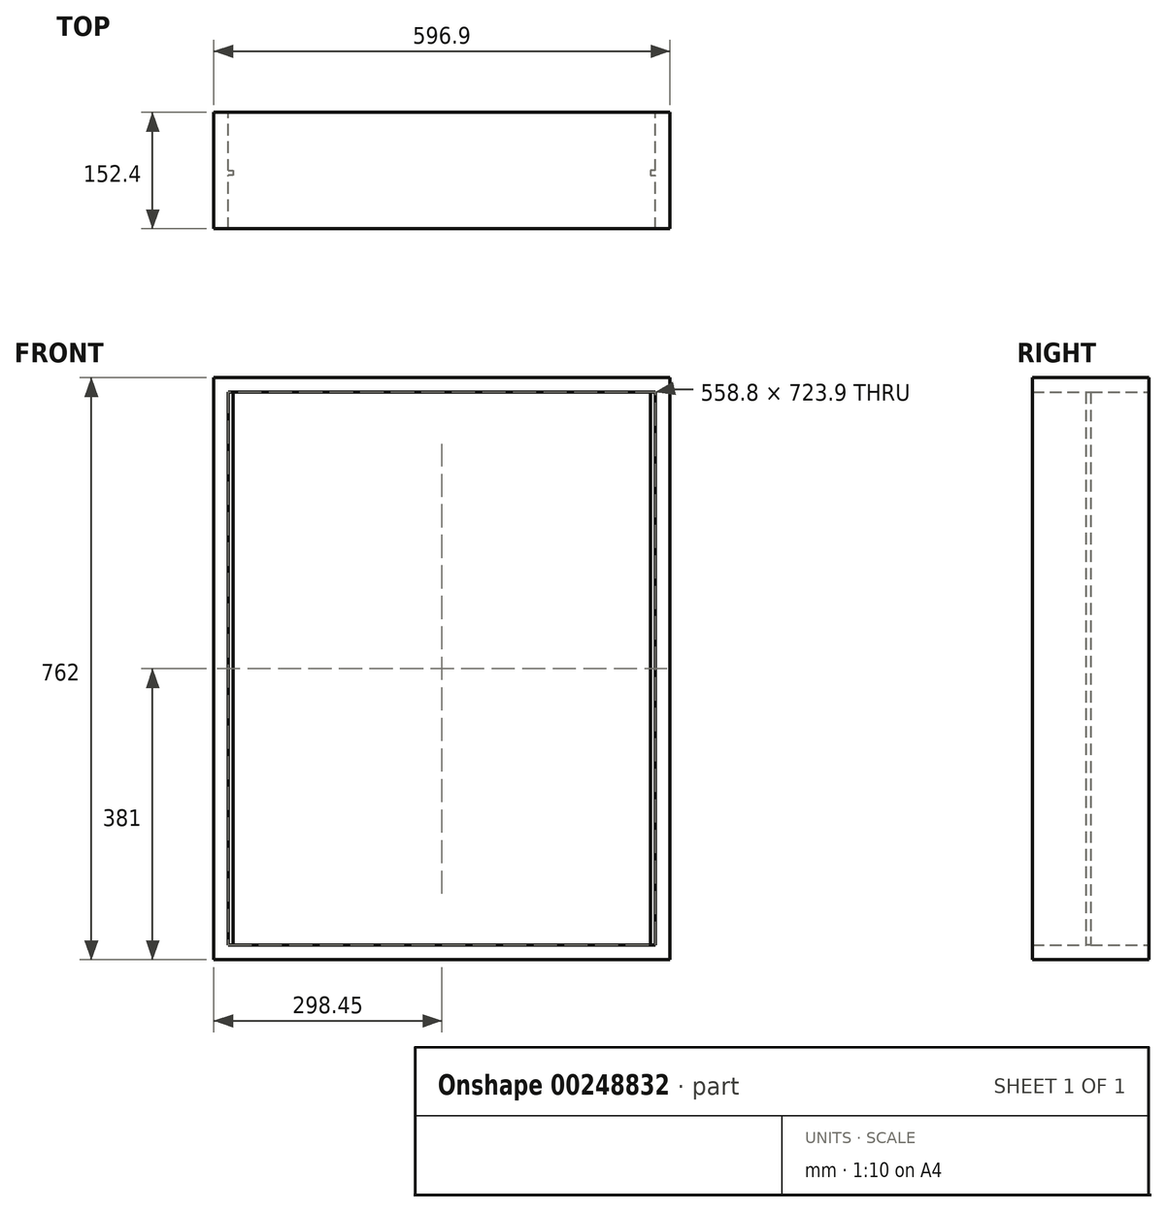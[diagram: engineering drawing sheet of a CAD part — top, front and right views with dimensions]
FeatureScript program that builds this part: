
annotation { "Feature Type Name" : "Feature", "Feature Type Description" : "" }
export const myFeature = defineFeature(function(context is Context, id is Id, definition is map)
    precondition{}
    {
        {
            var Q0;
            Q0=qCreatedBy(makeId("Front.planeOp"),FACE);
            var sketch = newSketch(context, id + "F0", { "sketchPlane" : qUnion([Q0])});
            skLineSegment(sketch, "E0.bottom", {"start": v(0, 0) * mm, "end": v(-558.8, 0) * mm});
            skLineSegment(sketch, "E0.top", {"start": v(0, 723.9) * mm, "end": v(-558.8, 723.9) * mm});
            skLineSegment(sketch, "E0.left", {"start": v(0, 0) * mm, "end": v(0, 723.9) * mm});
            skLineSegment(sketch, "E0.right", {"start": v(-558.8, 0) * mm, "end": v(-558.8, 723.9) * mm});
            skLineSegment(sketch, "E1.bottom", {"start": v(-577.85, 742.95) * mm, "end": v(19.05, 742.95) * mm});
            skLineSegment(sketch, "E1.top", {"start": v(-577.85, -19.05) * mm, "end": v(19.05, -19.05) * mm});
            skLineSegment(sketch, "E1.left", {"start": v(-577.85, 742.95) * mm, "end": v(-577.85, -19.05) * mm});
            skLineSegment(sketch, "E1.right", {"start": v(19.05, 742.95) * mm, "end": v(19.05, -19.05) * mm});
            skSolve(sketch);
        }
        {
            var Q0;
            Q0=makeQuery(id+"F0.imprint","IMPRINT",FACE,{"disambiguationData":[TD([[makeQuery(id+"F0.imprint","IMPRINT",EDGE,{"derivedFrom":sQuery(id+"F0.wireOp",EDGE,"E0.bottom")}),1.0]])]});
            extrude(context, id + "F1", {"entities" : qUnion([Q0]), "depth" : 152.4 * mm});
        }
        {
            var Q0;
            Q0=makeQuery(id+"F1.opExtrude","SWEPT_FACE",FACE,{"disambiguationData":[OSD([sQuery(id+"F0.wireOp",EDGE,"E0.bottom")])]});
            var sketch = newSketch(context, id + "F2", { "sketchPlane" : qUnion([Q0])});
            skLineSegment(sketch, "E2", {"start": v(-558.8, -76.2) * mm, "end": v(-552.45, -76.2) * mm});
            skLineSegment(sketch, "E3", {"start": v(-552.45, -76.2) * mm, "end": v(-552.45, -82.55) * mm});
            skLineSegment(sketch, "E4", {"start": v(-552.45, -82.55) * mm, "end": v(-558.8, -82.55) * mm});
            skLineSegment(sketch, "E5", {"start": v(-558.8, -82.55) * mm, "end": v(-558.8, -76.2) * mm});
            skLineSegment(sketch, "E6", {"start": v(0, -76.2) * mm, "end": v(-6.35, -76.2) * mm});
            skPoint(sketch, "E6.endSnap0", {"position": v(0, -76.2) * mm});
            skLineSegment(sketch, "E7", {"start": v(-6.35, -76.2) * mm, "end": v(-6.35, -82.55) * mm});
            skLineSegment(sketch, "E8", {"start": v(-6.35, -82.55) * mm, "end": v(0, -82.55) * mm});
            skLineSegment(sketch, "E9", {"start": v(0, -82.55) * mm, "end": v(0, -76.2) * mm});
            skSolve(sketch);
        }
        {
            var Q0;
            Q0=makeQuery(id+"F2.imprint","IMPRINT",FACE,{"disambiguationData":[TD([[makeQuery(id+"F2.imprint","IMPRINT",EDGE,{"derivedFrom":sQuery(id+"F2.wireOp",EDGE,"E2")}),-1.0]])]});
            var Q1;
            Q1=makeQuery(id+"F2.imprint","IMPRINT",FACE,{"disambiguationData":[TD([[makeQuery(id+"F2.imprint","IMPRINT",EDGE,{"derivedFrom":sQuery(id+"F2.wireOp",EDGE,"E6")}),1.0]])]});
            extrude(context, id + "F3", {"entities" : qUnion([Q0, Q1]), "operationType" : NewBodyOperationType.ADD, "endBound" : BoundingType.UP_TO_NEXT, "depth" : 25.4 * mm});
        }
    });
